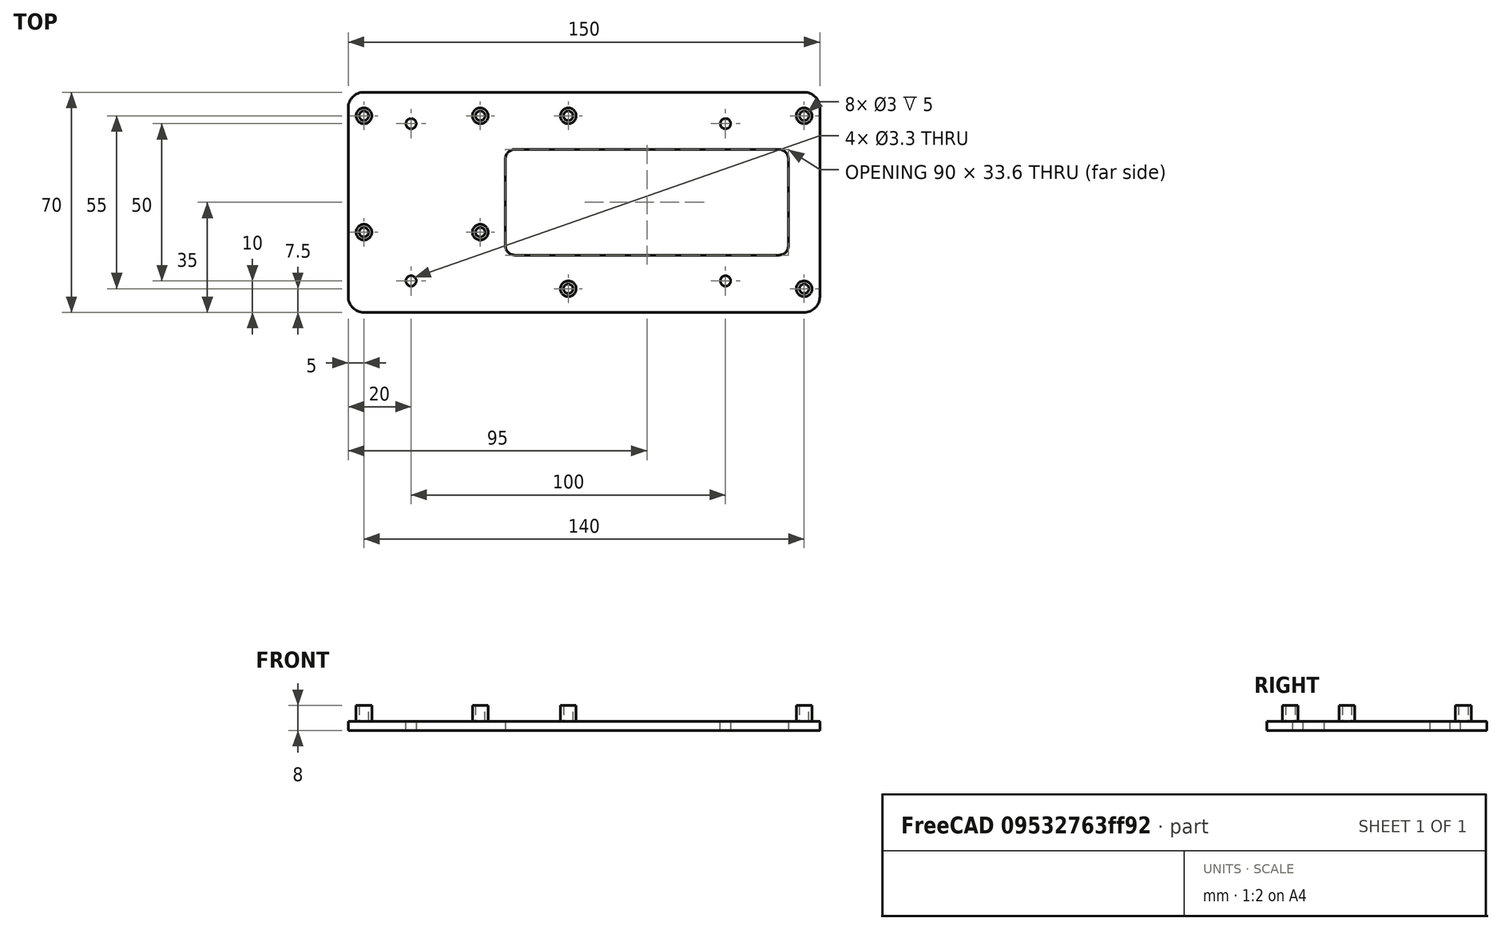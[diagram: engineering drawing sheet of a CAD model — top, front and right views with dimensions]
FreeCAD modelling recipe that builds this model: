
FCSTD DOCUMENT  (FreeCAD 0.19R23756 (Git))
Label: elite_component_bracket
License: All rights reserved
LicenseURL: http://en.wikipedia.org/wiki/All_rights_reserved
objects: Sketcher::SketchObject×4, PartDesign::Pad×2, PartDesign::Fillet×2, PartDesign::Pocket×2, Mesh::Feature×1, PartDesign::Body×1, TechDraw::DrawSVGTemplate×1, TechDraw::DrawViewPart×1, TechDraw::DrawPage×1
note: 17 computed .brp shape members not serialized (recipe doc carries the construction recipe); baked Part::Feature solids carry a one-line shape summary decoded from their .brp

FEATURE [Sketcher::SketchObject] Sketch
  FullyConstrained = true
  MapMode = 5
  Support = -> [XY_Plane]
  sketch-geometry (4):
    g0: LineSegment StartX=-75 StartY=35 StartZ=0 EndX=75 EndY=35 EndZ=0
    g1: LineSegment StartX=75 StartY=35 StartZ=0 EndX=75 EndY=-35 EndZ=0
    g2: LineSegment StartX=75 StartY=-35 StartZ=0 EndX=-75 EndY=-35 EndZ=0
    g3: LineSegment StartX=-75 StartY=-35 StartZ=0 EndX=-75 EndY=35 EndZ=0
  constraints (11):
    c: Coincident(g0,g1)
    c: Coincident(g1,g2)
    c: Coincident(g2,g3)
    c: Coincident(g3,g0)
    c: Horizontal(g0)
    c: Horizontal(g2)
    c: Vertical(g1)
    c: Vertical(g3)
    c: DistanceX(g0,g0) = 150
    c: DistanceY(g2,g0) = 70
    c: Symmetric(g0,g1,g-1)
FEATURE [PartDesign::Pad] Pad
  Direction = (1,1,1)
  Length = 3
  Length2 = 100
  Profile = -> Sketch
  Type = 0
FEATURE [Sketcher::SketchObject] Sketch001
  ExternalGeometry = -> [Pad]
  FullyConstrained = true
  MapMode = 5
  Placement = pos=(0,0,3) rot=(0,0,1;0rad)
  Support = -> [Pad]
  sketch-geometry (16):
    g0: Circle CenterX=-5 CenterY=27.5 CenterZ=0 NormalX=0 NormalY=0 NormalZ=1 AngleXU=0 Radius=1.5
    g1: Circle CenterX=-5 CenterY=27.5 CenterZ=0 NormalX=0 NormalY=0 NormalZ=1 AngleXU=0 Radius=2.5
    g2: Circle CenterX=70 CenterY=27.5 CenterZ=0 NormalX=0 NormalY=0 NormalZ=1 AngleXU=0 Radius=1.5
    g3: Circle CenterX=70 CenterY=27.5 CenterZ=0 NormalX=0 NormalY=0 NormalZ=1 AngleXU=0 Radius=2.5
    g4: Circle CenterX=-5 CenterY=-27.5 CenterZ=0 NormalX=0 NormalY=0 NormalZ=1 AngleXU=0 Radius=1.5
    g5: Circle CenterX=-5 CenterY=-27.5 CenterZ=0 NormalX=0 NormalY=0 NormalZ=1 AngleXU=0 Radius=2.5
    g6: Circle CenterX=70 CenterY=-27.5 CenterZ=0 NormalX=0 NormalY=0 NormalZ=1 AngleXU=0 Radius=1.5
    g7: Circle CenterX=70 CenterY=-27.5 CenterZ=0 NormalX=0 NormalY=0 NormalZ=1 AngleXU=0 Radius=2.5
    g8: Circle CenterX=-70 CenterY=27.5 CenterZ=0 NormalX=0 NormalY=0 NormalZ=1 AngleXU=0 Radius=1.5
    g9: Circle CenterX=-70 CenterY=27.5 CenterZ=0 NormalX=0 NormalY=0 NormalZ=1 AngleXU=0 Radius=2.5
    g10: Circle CenterX=-70 CenterY=-9.5 CenterZ=0 NormalX=0 NormalY=0 NormalZ=1 AngleXU=0 Radius=1.5
    g11: Circle CenterX=-70 CenterY=-9.5 CenterZ=0 NormalX=0 NormalY=0 NormalZ=1 AngleXU=0 Radius=2.5
    g12: Circle CenterX=-33 CenterY=-9.5 CenterZ=0 NormalX=0 NormalY=0 NormalZ=1 AngleXU=0 Radius=1.5
    g13: Circle CenterX=-33 CenterY=-9.5 CenterZ=0 NormalX=0 NormalY=0 NormalZ=1 AngleXU=0 Radius=2.5
    g14: Circle CenterX=-33 CenterY=27.5 CenterZ=0 NormalX=0 NormalY=0 NormalZ=1 AngleXU=0 Radius=1.5
    g15: Circle CenterX=-33 CenterY=27.5 CenterZ=0 NormalX=0 NormalY=0 NormalZ=1 AngleXU=0 Radius=2.5
  constraints (39):
    c: Coincident(g0,g1)
    c: Coincident(g3,g2)
    c: Coincident(g4,g5)
    c: Coincident(g6,g7)
    c: Radius(g2) = 1.5
    c: Equal(g2,g4)
    c: Equal(g2,g6)
    c: Radius(g3) = 2.5
    c: Equal(g1,g7)
    c: Equal(g7,g5)
    c: Equal(g5,g3)
    c: DistanceY(g6,g2) = 55
    c: Vertical(g2,g6)
    c: Horizontal(g0,g2)
    c: Horizontal(g4,g6)
    c: DistanceX(g0,g2) = 75
    c: Coincident(g8,g9)
    c: Coincident(g15,g14)
    c: Coincident(g13,g12)
    c: Coincident(g11,g10)
    c: Vertical(g10,g8)
    c: Horizontal(g12,g10)
    c: Horizontal(g14,g8)
    c: Radius(g8) = 1.5
    c: Equal(g8,g14)
    c: Equal(g14,g12)
    c: Equal(g12,g10)
    c: Radius(g9) = 2.5
    c: Equal(g11,g13)
    c: Equal(g13,g15)
    c: Equal(g15,g9)
    c: Symmetric(g0,g4,g-1)
    c: DistanceX(g8,g14) = 37
    c: DistanceY(g10,g8) = 37
    c: DistanceX(g2,g-4) = 5
    c: DistanceX(g-3,g10) = 5
    c: Equal(g0,g2)
    c: Horizontal(g14,g0)
    c: Vertical(g12,g14)
FEATURE [PartDesign::Pad] Pad001
  BaseFeature = -> Pad
  Direction = (1,1,1)
  Length = 5
  Length2 = 100
  Profile = -> Sketch001
  Type = 0
FEATURE [PartDesign::Fillet] Fillet
  Base = -> Pad001 [Edge8,Edge5,Edge1,Edge2]
  BaseFeature = -> Pad001
  Radius = 5
  SupportTransform = false
FEATURE [Sketcher::SketchObject] Sketch002
  FullyConstrained = true
  MapMode = 5
  Placement = pos=(0,0,3) rot=(0,0,1;0rad)
  Support = -> [Fillet]
  sketch-geometry (4):
    g0: LineSegment StartX=-25 StartY=16.8 StartZ=0 EndX=65 EndY=16.8 EndZ=0
    g1: LineSegment StartX=65 StartY=16.8 StartZ=0 EndX=65 EndY=-16.8 EndZ=0
    g2: LineSegment StartX=65 StartY=-16.8 StartZ=0 EndX=-25 EndY=-16.8 EndZ=0
    g3: LineSegment StartX=-25 StartY=-16.8 StartZ=0 EndX=-25 EndY=16.8 EndZ=0
  constraints (11):
    c: Coincident(g0,g1)
    c: Coincident(g1,g2)
    c: Coincident(g2,g3)
    c: Coincident(g3,g0)
    c: Horizontal(g0)
    c: Horizontal(g2)
    c: Vertical(g3)
    c: Symmetric(g0,g1,g-1)
    c: DistanceY(g1,g0) = 33.6
    c: DistanceX(g0,g0) = 90
    c: DistanceX(g2,g-1) = 25
FEATURE [PartDesign::Pocket] Pocket
  BaseFeature = -> Fillet
  Length = 5
  Length2 = 100
  Profile = -> Sketch002
  Type = 0
FEATURE [PartDesign::Fillet] Fillet001
  Base = -> Pocket [Edge44,Edge42,Edge41,Edge43]
  BaseFeature = -> Pocket
  Radius = 3
  SupportTransform = false
FEATURE [Mesh::Feature] Mesh  label="v1, std mesh"
FEATURE [Sketcher::SketchObject] Sketch003
  ExternalGeometry = -> [Fillet001]
  FullyConstrained = true
  MapMode = 5
  Placement = pos=(0,0,3) rot=(0,0,1;0rad)
  Support = -> [Fillet001]
  sketch-geometry (4):
    g0: Circle CenterX=-55 CenterY=25 CenterZ=0 NormalX=0 NormalY=0 NormalZ=1 AngleXU=0 Radius=1.65
    g1: Circle CenterX=45 CenterY=25 CenterZ=0 NormalX=0 NormalY=0 NormalZ=1 AngleXU=0 Radius=1.65
    g2: Circle CenterX=45 CenterY=-25 CenterZ=0 NormalX=0 NormalY=0 NormalZ=1 AngleXU=0 Radius=1.65
    g3: Circle CenterX=-55 CenterY=-25 CenterZ=0 NormalX=0 NormalY=0 NormalZ=1 AngleXU=0 Radius=1.65
  constraints (11):
    c: Radius(g3) = 1.65
    c: Equal(g2,g3)
    c: Equal(g1,g3)
    c: Equal(g0,g3)
    c: Horizontal(g3,g2)
    c: Horizontal(g0,g1)
    c: Vertical(g1,g2)
    c: DistanceX(g2,g-3) = 30
    c: DistanceX(g3,g2) = 100
    c: DistanceY(g3,g0) = 50
    c: Symmetric(g3,g0,g-1)
FEATURE [PartDesign::Pocket] Pocket001
  BaseFeature = -> Fillet001
  Length = 5
  Length2 = 100
  Profile = -> Sketch003
  Type = 0
FEATURE [PartDesign::Body] Body
  Group = -> [Sketch,Pad,Sketch001,Pad001,Fillet,Sketch002,Pocket,Fillet001,Sketch003,Pocket001]
  Origin = -> Origin
  Tip = -> Pocket001
FEATURE [TechDraw::DrawSVGTemplate] Template
  EditableTexts = Code=v 1; CompanyName=BJV.US; DrawingNumber=template; DrawingTitle1=Elite Controller Bracket; DrawnBy=Ben; Revision=r1; Scale=scale 1:1; Sheet=Sheet 1 of 1
  Height = 215.9
  Orientation = 1
  Width = 279.4
FEATURE [TechDraw::DrawViewPart] View
  CoarseView = false
  Direction = (0,0,-1)
  Focus = 100
  HardHidden = false
  IsoCount = 0
  IsoHidden = false
  IsoVisible = false
  LockPosition = false
  Perspective = false
  Rotation = 0
  ScaleType = 0
  SeamHidden = false
  SeamVisible = true
  SmoothHidden = false
  SmoothVisible = true
  Source = -> [Pocket001]
  X = 139.7
  XDirection = (1,0,0)
  Y = 127.95
FEATURE [TechDraw::DrawPage] Page
  KeepUpdated = true
  NextBalloonIndex = 1
  ProjectionType = 0
  Template = -> Template
  Views = -> [View]
